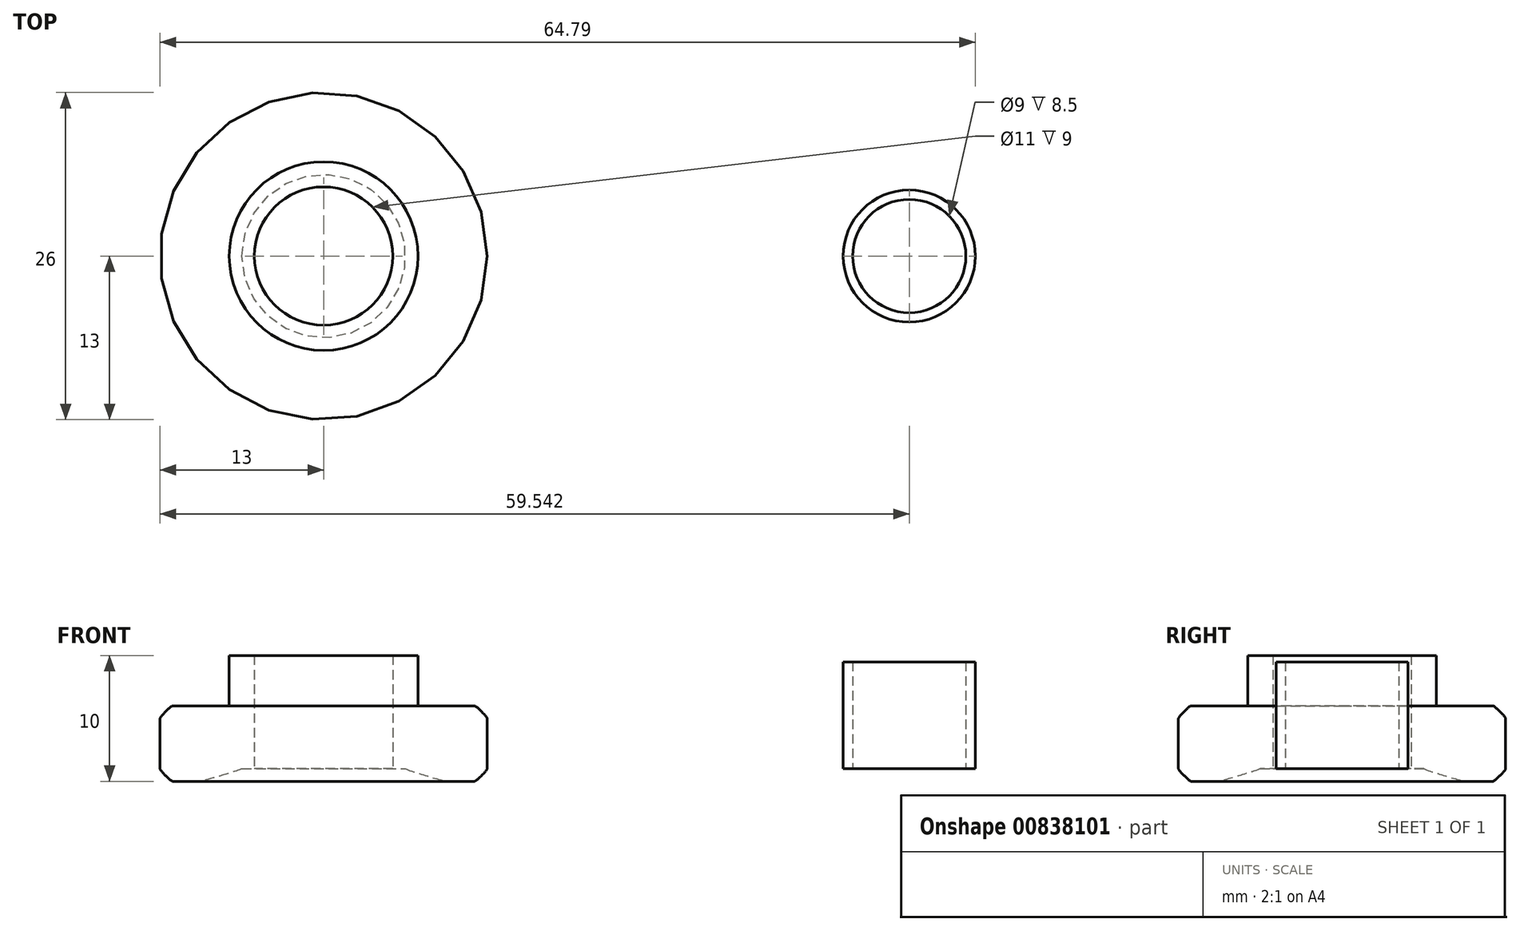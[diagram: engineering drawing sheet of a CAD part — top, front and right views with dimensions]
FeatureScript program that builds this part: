
annotation { "Feature Type Name" : "Feature", "Feature Type Description" : "" }
export const myFeature = defineFeature(function(context is Context, id is Id, definition is map)
    precondition{}
    {
        {
            var Q0;
            Q0=qCreatedBy(makeId("Top.planeOp"),FACE);
            var sketch = newSketch(context, id + "F0", { "sketchPlane" : qUnion([Q0])});
            skCircle(sketch, "E0", {"center": v(0, 0) * mm, "radius": 13 * mm});
            skCircle(sketch, "E1", {"center": v(0, 0) * mm, "radius": 5.5 * mm});
            skSolve(sketch);
        }
        {
            var Q0;
            Q0=makeQuery(id+"F0.imprint","IMPRINT",FACE,{"disambiguationData":[TD([[makeQuery(id+"F0.imprint","IMPRINT",EDGE,{"derivedFrom":sQuery(id+"F0.wireOp",EDGE,"E0")}),1.0]])]});
            extrude(context, id + "F1", {"entities" : qUnion([Q0]), "depth" : 5 * mm, "offsetDistance" : 25 * mm});
        }
        {
            var Q0;
            Q0=qCreatedBy(makeId("Top.planeOp"),FACE);
            var sketch = newSketch(context, id + "F2", { "sketchPlane" : qUnion([Q0])});
            skCircle(sketch, "E2", {"center": v(46.54, 0) * mm, "radius": 4.5 * mm});
            skCircle(sketch, "E3", {"center": v(46.54, 0) * mm, "radius": 5.25 * mm});
            skSolve(sketch);
        }
        {
            var Q0;
            Q0=makeQuery(id+"F2.imprint","IMPRINT",FACE,{"disambiguationData":[TD([[makeQuery(id+"F2.imprint","IMPRINT",EDGE,{"derivedFrom":sQuery(id+"F2.wireOp",EDGE,"E2")}),-1.0]])]});
            extrude(context, id + "F3", {"entities" : qUnion([Q0]), "depth" : 8.5 * mm, "offsetDistance" : 25 * mm});
        }
        {
            var Q0;
            Q0=makeQuery(id+"F1.opExtrude","CAP_FACE",FACE,{"disambiguationData":[OSD([sQuery(id+"F0.wireOp",EDGE,"E0"),sQuery(id+"F0.wireOp",EDGE,"E1")])],"isStart":false});
            var sketch = newSketch(context, id + "F4", { "sketchPlane" : qUnion([Q0])});
            skCircle(sketch, "E4", {"center": v(0, 0) * mm, "radius": 7.5 * mm});
            skCircle(sketch, "E5", {"center": v(0, 0) * mm, "radius": 5.5 * mm});
            skSolve(sketch);
        }
        {
            var Q0;
            Q0=makeQuery(id+"F4.imprint","IMPRINT",FACE,{"disambiguationData":[TD([[makeQuery(id+"F4.imprint","IMPRINT",EDGE,{"derivedFrom":sQuery(id+"F4.wireOp",EDGE,"E4")}),1.0]])]});
            extrude(context, id + "F5", {"entities" : qUnion([Q0]), "operationType" : NewBodyOperationType.ADD, "depth" : 4 * mm, "offsetDistance" : 25 * mm});
        }
        {
            var Q0;
            Q0=makeQuery(id+"F1.opExtrude","CAP_FACE",FACE,{"disambiguationData":[OSD([sQuery(id+"F0.wireOp",EDGE,"E0"),sQuery(id+"F0.wireOp",EDGE,"E1")])],"isStart":true});
            var sketch = newSketch(context, id + "F6", { "sketchPlane" : qUnion([Q0])});
            skCircle(sketch, "E6", {"center": v(0, 0) * mm, "radius": 6.5 * mm});
            skSolve(sketch);
        }
        {
            var Q0;
            Q0=makeQuery(id+"F6.imprint","IMPRINT",FACE,{"disambiguationData":[TD([[makeQuery(id+"F6.imprint","IMPRINT",EDGE,{"derivedFrom":sQuery(id+"F6.wireOp",EDGE,"E6")}),-1.0]])]});
            extrude(context, id + "F7", {"entities" : qUnion([Q0]), "operationType" : NewBodyOperationType.ADD, "depth" : 1 * mm, "offsetDistance" : 25 * mm});
        }
        {
            var Q0;
            Q0=makeQuery(id+"F7.opExtrude","CAP_EDGE",EDGE,{"disambiguationData":[OSD([sQuery(id+"F0.wireOp",EDGE,"E0")])],"isStart":false});
            var Q1;
            Q1=makeQuery(id+"F1.opExtrude","CAP_EDGE",EDGE,{"disambiguationData":[OSD([sQuery(id+"F0.wireOp",EDGE,"E0")])],"isStart":false});
            fillet(context, id + "F8", {"entities" : qUnion([Q0, Q1]), "radius" : 1 * mm, "tangentPropagation" : true, "rho" : 0.1, "crossSection" : FilletCrossSection.CONIC, "allowEdgeOverflow" : false});
        }
        {
            var Q0;
            Q0=makeQuery(id+"F7.opExtrude","CAP_EDGE",EDGE,{"disambiguationData":[OSD([sQuery(id+"F6.wireOp",EDGE,"E6")])],"isStart":false});
            fillet(context, id + "F9", {"entities" : qUnion([Q0]), "radius" : 6 * mm, "tangentPropagation" : true, "rho" : 0.1, "crossSection" : FilletCrossSection.CONIC, "allowEdgeOverflow" : false});
        }
    });
